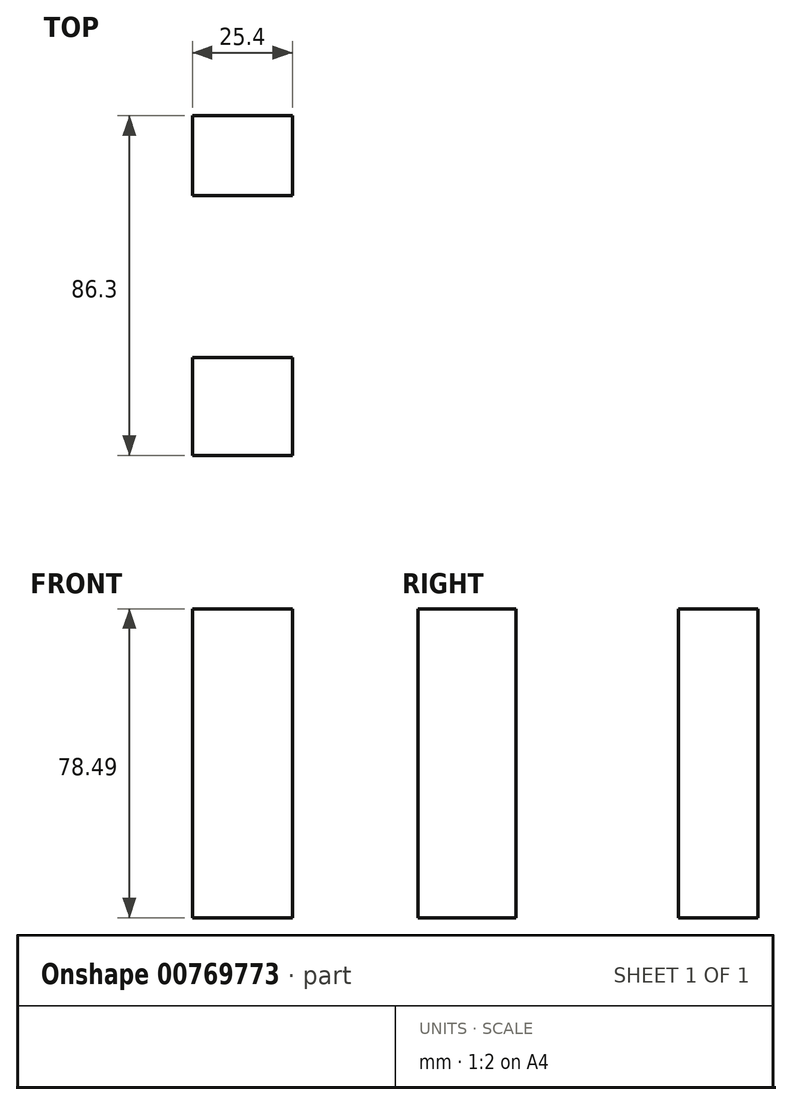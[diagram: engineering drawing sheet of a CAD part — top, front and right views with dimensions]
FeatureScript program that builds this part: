
annotation { "Feature Type Name" : "Feature", "Feature Type Description" : "" }
export const myFeature = defineFeature(function(context is Context, id is Id, definition is map)
    precondition{}
    {
        {
            var Q0;
            Q0=qCreatedBy(makeId("Right.planeOp"),FACE);
            var sketch = newSketch(context, id + "F0", { "sketchPlane" : qUnion([Q0])});
            skLineSegment(sketch, "E0.bottom", {"start": v(-45.46, 57) * mm, "end": v(40.84, 57) * mm});
            skLineSegment(sketch, "E0.top", {"start": v(-45.46, -21.49) * mm, "end": v(40.84, -21.49) * mm});
            skLineSegment(sketch, "E0.left", {"start": v(-45.46, 57) * mm, "end": v(-45.46, -21.49) * mm});
            skLineSegment(sketch, "E0.right", {"start": v(40.84, 57) * mm, "end": v(40.84, -21.49) * mm});
            skLineSegment(sketch, "E1.bottom", {"start": v(20.6, -61.61) * mm, "end": v(-20.6, -61.61) * mm});
            skLineSegment(sketch, "E1.top", {"start": v(20.6, 61.61) * mm, "end": v(-20.6, 61.61) * mm});
            skLineSegment(sketch, "E1.left", {"start": v(20.6, -61.61) * mm, "end": v(20.6, 61.61) * mm});
            skLineSegment(sketch, "E1.right", {"start": v(-20.6, -61.61) * mm, "end": v(-20.6, 61.61) * mm});
            skPoint(sketch, "E1.middle", {"position": v(0, 0) * mm});
            skLineSegment(sketch, "E2.bottom", {"start": v(-185.38, 19) * mm, "end": v(-196.03, 19) * mm});
            skLineSegment(sketch, "E2.top", {"start": v(-185.38, 17.58) * mm, "end": v(-196.03, 17.58) * mm});
            skLineSegment(sketch, "E2.left", {"start": v(-185.38, 19) * mm, "end": v(-185.38, 17.58) * mm});
            skLineSegment(sketch, "E2.right", {"start": v(-196.03, 19) * mm, "end": v(-196.03, 17.58) * mm});
            skPoint(sketch, "E2.middle", {"position": v(-190.7, 18.29) * mm});
            skSolve(sketch);
        }
        {
            var Q0;
            {var subQ0=sQuery(id+"F0.wireOp",EDGE,"E0.left");Q0=makeQuery(id+"F0.imprint","IMPRINT",FACE,{"disambiguationData":[TD([[makeQuery(id+"F0.imprint","IMPRINT",EDGE,{"derivedFrom":subQ0}),1.0]])]});}
            var Q1;
            {var subQ0=sQuery(id+"F0.wireOp",EDGE,"E0.right");Q1=makeQuery(id+"F0.imprint","IMPRINT",FACE,{"disambiguationData":[TD([[makeQuery(id+"F0.imprint","IMPRINT",EDGE,{"derivedFrom":subQ0}),-1.0]])]});}
            extrude(context, id + "F1", {"entities" : qUnion([Q0, Q1]), "depth" : 25.4 * mm, "offsetDistance" : 25.4 * mm});
        }
    });
